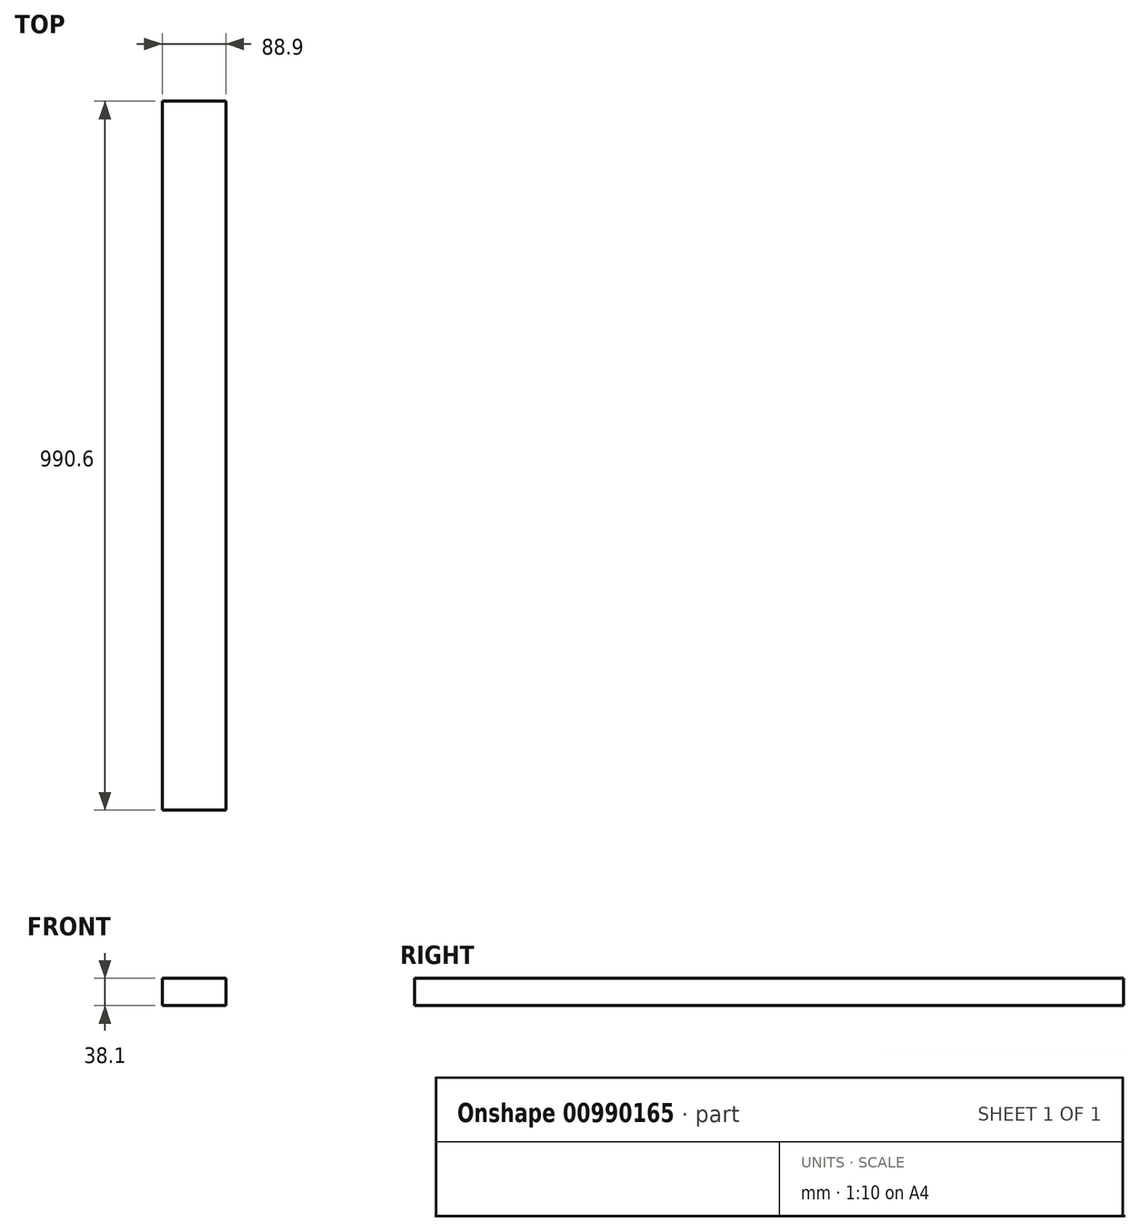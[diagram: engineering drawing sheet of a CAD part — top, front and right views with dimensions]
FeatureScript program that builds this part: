
annotation { "Feature Type Name" : "Feature", "Feature Type Description" : "" }
export const myFeature = defineFeature(function(context is Context, id is Id, definition is map)
    precondition{}
    {
        {
            assignVariable(context, id + "F0", {"name" : "w", "anyValue" : 38.1 * mm});
        }
        {
            var Q0;
            Q0=qCreatedBy(makeId("Top.planeOp"),FACE);
            var sketch = newSketch(context, id + "F1", { "sketchPlane" : qUnion([Q0])});
            skLineSegment(sketch, "E0.bottom", {"start": v(44.45, 495.3) * mm, "end": v(-44.45, 495.3) * mm});
            skLineSegment(sketch, "E0.top", {"start": v(44.45, -495.3) * mm, "end": v(-44.45, -495.3) * mm});
            skLineSegment(sketch, "E0.left", {"start": v(44.45, 495.3) * mm, "end": v(44.45, -495.3) * mm});
            skLineSegment(sketch, "E0.right", {"start": v(-44.45, 495.3) * mm, "end": v(-44.45, -495.3) * mm});
            skPoint(sketch, "E0.middle", {"position": v(0, 0) * mm});
            skSolve(sketch);
        }
        {
            var Q0;
            Q0=qSketchRegion(id+"F1",true);
            extrude(context, id + "F2", {"entities" : qUnion([Q0]), "depth" : getVariable(context, 'w'), "offsetDistance" : 25.4 * mm});
        }
    });
